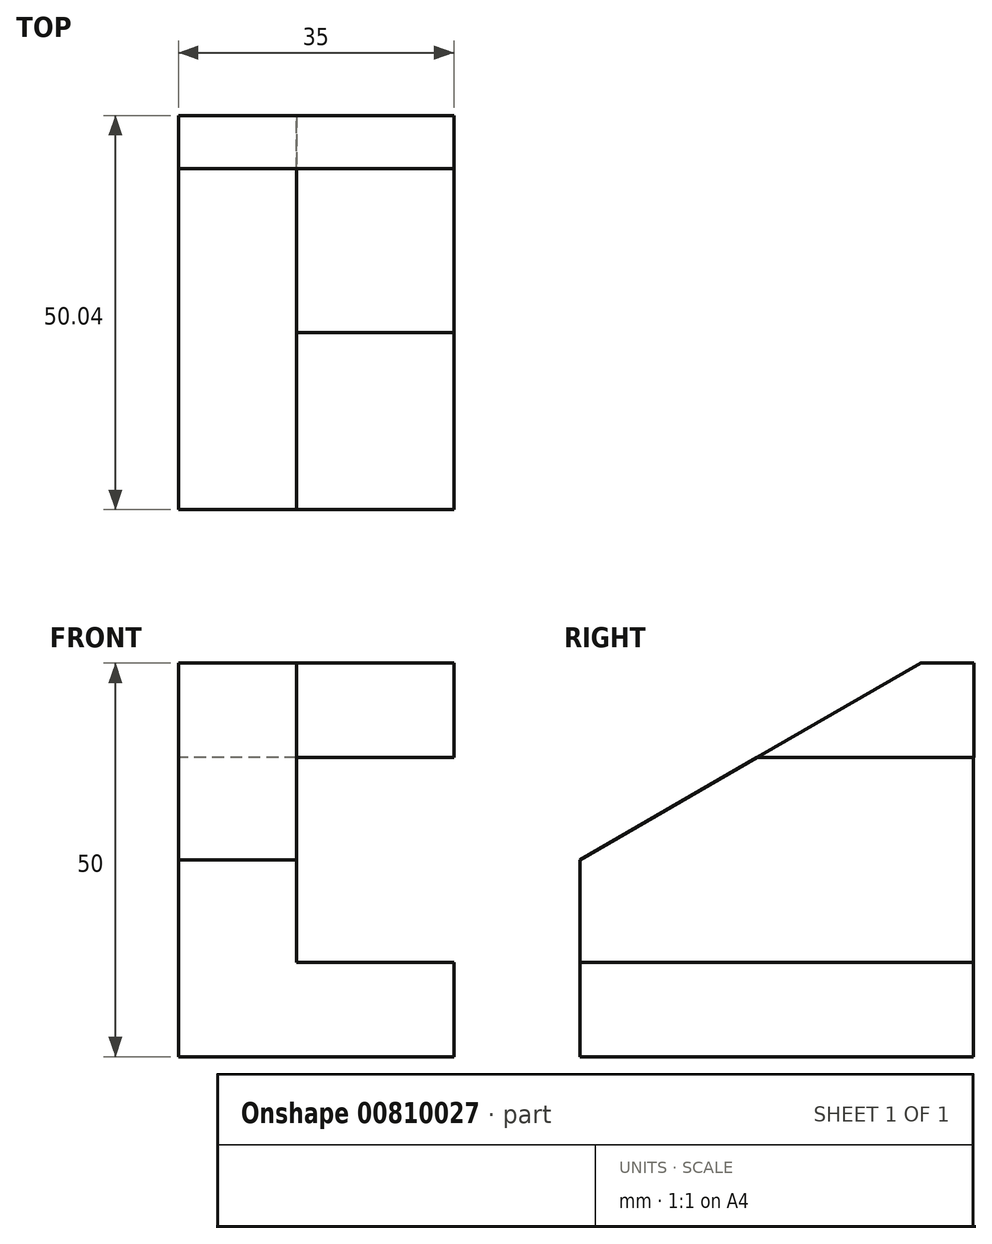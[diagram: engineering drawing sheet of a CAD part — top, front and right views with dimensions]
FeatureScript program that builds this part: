
annotation { "Feature Type Name" : "Feature", "Feature Type Description" : "" }
export const myFeature = defineFeature(function(context is Context, id is Id, definition is map)
    precondition{}
    {
        {
            var Q0;
            Q0=qCreatedBy(makeId("Right.planeOp"),FACE);
            var sketch = newSketch(context, id + "F0", { "sketchPlane" : qUnion([Q0])});
            skLineSegment(sketch, "E0.bottom", {"start": v(-25, 25) * mm, "end": v(25, 25) * mm});
            skLineSegment(sketch, "E0.top", {"start": v(-25, -25) * mm, "end": v(25, -25) * mm});
            skLineSegment(sketch, "E0.left", {"start": v(-25, 25) * mm, "end": v(-25, -25) * mm});
            skLineSegment(sketch, "E0.right", {"start": v(25, 25) * mm, "end": v(25, -25) * mm});
            skSolve(sketch);
        }
        {
            var Q0;
            Q0 = qSketchRegion(id + "F0", true);
            extrude(context, id + "F1", {"entities" : qUnion([Q0]), "depth" : 15 * mm, "offsetDistance" : 25 * mm});
        }
        {
            var Q0;
            Q0=makeQuery(id+"F1.opExtrude","SWEPT_EDGE",EDGE,{"disambiguationData":[OSD([sQuery(id+"F0.wireOp",EDGE,"E0.bottom"),sQuery(id+"F0.wireOp",EDGE,"E0.left")])]});
            chamfer(context, id + "F2", {"entities" : qUnion([Q0]), "chamferType" : ChamferType.OFFSET_ANGLE, "width" : 25 * mm, "oppositeDirection" : false, "angle" : 60 * degree, "tangentPropagation" : true});
        }
        {
            var Q0;
            Q0=qCreatedBy(makeId("Right.planeOp"),FACE);
            var sketch = newSketch(context, id + "F3", { "sketchPlane" : qUnion([Q0])});
            skLineSegment(sketch, "E1", {"start": v(25.04, 13) * mm, "end": v(-2.48, 13) * mm});
            skLineSegment(sketch, "E2", {"start": v(25.04, 13) * mm, "end": v(25.04, 25) * mm});
            skLineSegment(sketch, "E3", {"start": v(25.04, 25) * mm, "end": v(18.34, 25) * mm});
            skLineSegment(sketch, "E4", {"start": v(18.34, 25) * mm, "end": v(-2.48, 13) * mm});
            skSolve(sketch);
        }
        {
            var Q0;
            Q0 = qSketchRegion(id + "F3", true);
            extrude(context, id + "F4", {"entities" : qUnion([Q0]), "operationType" : NewBodyOperationType.ADD, "depth" : 35 * mm, "offsetDistance" : 25 * mm});
        }
        {
            var Q0;
            Q0=qCreatedBy(makeId("Right.planeOp"),FACE);
            var sketch = newSketch(context, id + "F5", { "sketchPlane" : qUnion([Q0])});
            skLineSegment(sketch, "E5", {"start": v(-25, -25) * mm, "end": v(-25, -13) * mm});
            skLineSegment(sketch, "E6.bottom", {"start": v(-25, -25) * mm, "end": v(25, -25) * mm});
            skLineSegment(sketch, "E6.top", {"start": v(-25, -13) * mm, "end": v(25, -13) * mm});
            skLineSegment(sketch, "E6.right", {"start": v(25, -25) * mm, "end": v(25, -13) * mm});
            skSolve(sketch);
        }
        {
            var Q0;
            Q0 = qSketchRegion(id + "F5", true);
            extrude(context, id + "F6", {"entities" : qUnion([Q0]), "operationType" : NewBodyOperationType.ADD, "depth" : 35 * mm, "offsetDistance" : 25 * mm});
        }
    });
